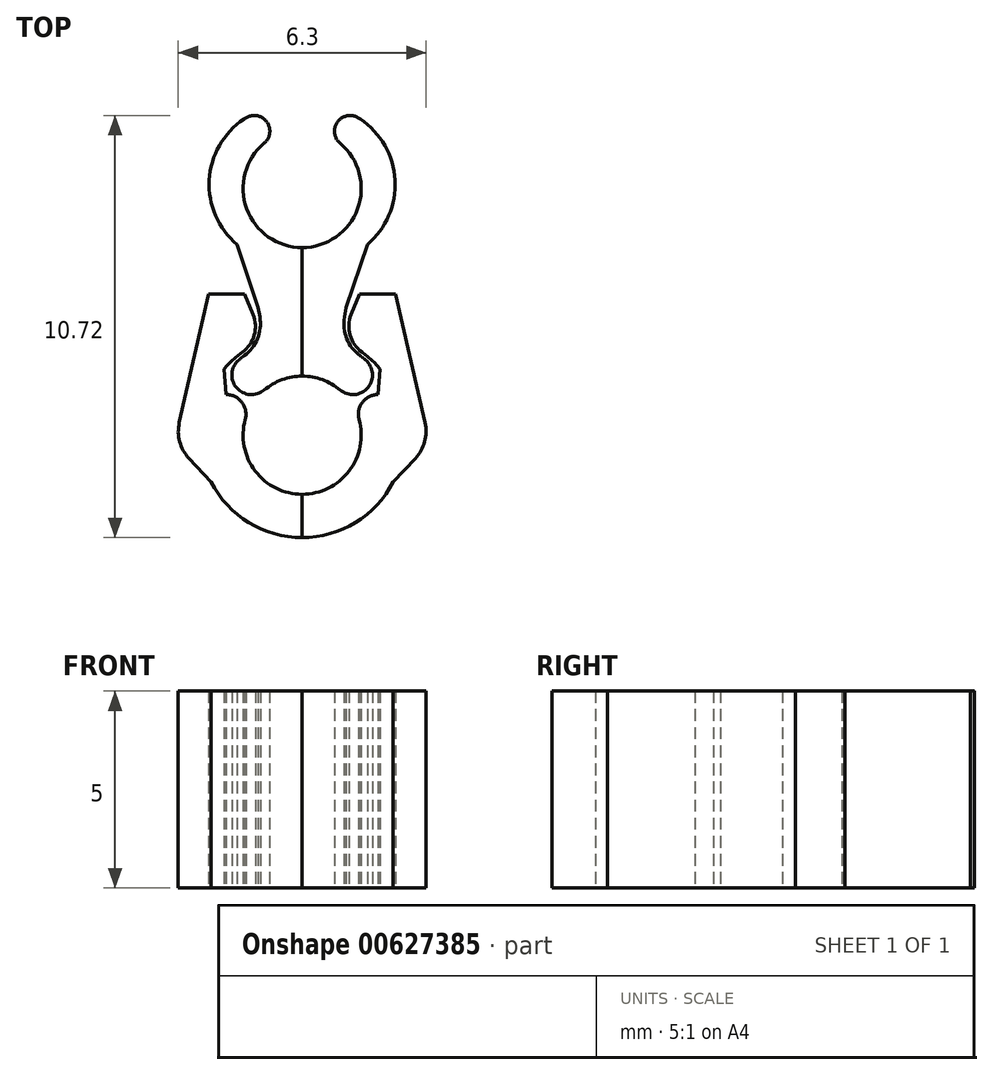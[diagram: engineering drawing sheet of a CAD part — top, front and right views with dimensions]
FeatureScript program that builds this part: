
annotation { "Feature Type Name" : "Feature", "Feature Type Description" : "" }
export const myFeature = defineFeature(function(context is Context, id is Id, definition is map)
    precondition{}
    {
        {
            var Q0;
            Q0=qCreatedBy(makeId("Top.planeOp"),FACE);
            var sketch = newSketch(context, id + "F0", { "sketchPlane" : qUnion([Q0])});
            skArc(sketch, "E0", {"start": v(-1.45, 0.4) * mm, "mid": v(-1.2, -0.9) * mm, "end": v(0, -1.5) * mm});
            skArc(sketch, "E1", {"start": v(-2.4, 0.67) * mm, "mid": v(-2.43, -0.6) * mm, "end": v(-1.82, -1.7) * mm});
            skPoint(sketch, "E2.orphan", {"position": v(0, 0.65) * mm});
            skLineSegment(sketch, "E3", {"start": v(0, 2) * mm, "end": v(0, 0) * mm});
            skArc(sketch, "E4.trimOffspring", {"start": v(-1.47, 2.02) * mm, "mid": v(-1.54, 1.97) * mm, "end": v(-1.6, 1.92) * mm});
            skArc(sketch, "E5.trimOffspring", {"start": v(0, 1.5) * mm, "mid": v(-0.51, 1.4) * mm, "end": v(-0.96, 1.15) * mm});
            skLineSegment(sketch, "E6", {"start": v(0, 0) * mm, "end": v(-0.96, 1.15) * mm, "construction": true});
            skArc(sketch, "E7", {"start": v(-1.6, 1.92) * mm, "mid": v(-1.67, 1.21) * mm, "end": v(-0.96, 1.15) * mm});
            skLineSegment(sketch, "E8", {"start": v(0, 0) * mm, "end": v(-2.4, 0.67) * mm, "construction": true});
            skArc(sketch, "E9", {"start": v(-1.45, 0.4) * mm, "mid": v(-1.53, 0.83) * mm, "end": v(-1.93, 1.03) * mm});
            skArc(sketch, "E10", {"start": v(-0.97, 2.41) * mm, "mid": v(-1.1, 2.35) * mm, "end": v(-1.23, 2.29) * mm});
            skPoint(sketch, "E11", {"position": v(0, 2.6) * mm});
            skLineSegment(sketch, "E12", {"start": v(-1.46, 3.59) * mm, "end": v(-1.25, 3.07) * mm, "construction": true});
            skLineSegment(sketch, "E13", {"start": v(-1.07, 3) * mm, "end": v(-1.12, 3.25) * mm});
            skLineSegment(sketch, "E14", {"start": v(-1.12, 3.25) * mm, "end": v(-3.54, 6.27) * mm, "construction": true});
            skLineSegment(sketch, "E15", {"start": v(-3.54, 6.27) * mm, "end": v(0.86, 6.27) * mm, "construction": true});
            skLineSegment(sketch, "E16", {"start": v(-1.46, 3.59) * mm, "end": v(-2.37, 3.59) * mm});
            skLineSegment(sketch, "E17", {"start": v(-2.37, 3.59) * mm, "end": v(-3.12, 0.32) * mm});
            skLineSegment(sketch, "E18", {"start": v(-2.88, -0.59) * mm, "end": v(-1.82, -1.7) * mm});
            skLineSegment(sketch, "E19", {"start": v(-0.98, 2.43) * mm, "end": v(-1.08, 2.65) * mm});
            skArc(sketch, "E20.trimOffspring", {"start": v(-1.52, 2.11) * mm, "mid": v(-1.76, 1.91) * mm, "end": v(-1.98, 1.68) * mm});
            skPoint(sketch, "E21.newPointB", {"position": v(-3.54, 8.6) * mm});
            skArc(sketch, "E21.filletArc", {"start": v(-1.52, 2.11) * mm, "mid": v(-1.22, 2.54) * mm, "end": v(-1.25, 3.07) * mm});
            skLineSegment(sketch, "E22", {"start": v(-1.99, 2.76) * mm, "end": v(-0.97, 2.13) * mm, "construction": true});
            skPoint(sketch, "E23", {"position": v(-1.3, 2.34) * mm});
            skArc(sketch, "E24.filletArc", {"start": v(-1.47, 2.02) * mm, "mid": v(-1.13, 2.45) * mm, "end": v(-1.07, 3) * mm});
            skPoint(sketch, "E25", {"position": v(-1.22, 2.28) * mm});
            skLineSegment(sketch, "E26.trimOffspring", {"start": v(-1.25, 3.07) * mm, "end": v(-1.46, 3.59) * mm});
            skLineSegment(sketch, "E27", {"start": v(0, 3.05) * mm, "end": v(0, 1.5) * mm});
            skPoint(sketch, "E28.visualSharp", {"position": v(-2.28, 1.03) * mm});
            skPoint(sketch, "E29.visualSharp", {"position": v(-3.24, -0.2) * mm});
            skArc(sketch, "E29.filletArc", {"start": v(-3.12, 0.32) * mm, "mid": v(-3.11, -0.16) * mm, "end": v(-2.88, -0.59) * mm});
            skArc(sketch, "E30", {"start": v(-0.96, 7.42) * mm, "mid": v(-0.63, 4.9) * mm, "end": v(1.5, 6.27) * mm});
            skLineSegment(sketch, "E31", {"start": v(-1.12, 3.25) * mm, "end": v(-1.66, 4.84) * mm});
            skLineSegment(sketch, "E32", {"start": v(0, 4.77) * mm, "end": v(0, 3.05) * mm});
            skLineSegment(sketch, "E33", {"start": v(0, 6.27) * mm, "end": v(-1.48, 8.03) * mm, "construction": true});
            skArc(sketch, "E34", {"start": v(-0.96, 7.42) * mm, "mid": v(-0.91, 7.98) * mm, "end": v(-1.48, 8.03) * mm});
            skLineSegment(sketch, "E35", {"start": v(0, 4.77) * mm, "end": v(0, 7.72) * mm});
            skArc(sketch, "E36.trimOffspring", {"start": v(-1.48, 8.03) * mm, "mid": v(-2.36, 6.48) * mm, "end": v(-1.66, 4.84) * mm});
            skLineSegment(sketch, "E37", {"start": v(0, -2.6) * mm, "end": v(0, -2.5) * mm});
            skArc(sketch, "E38.trimOffspring", {"start": v(0, 2.6) * mm, "mid": v(-0.5, 2.55) * mm, "end": v(-0.97, 2.41) * mm});
            skLineSegment(sketch, "E39.trimOffspring", {"start": v(0, -1.5) * mm, "end": v(0, -2.5) * mm});
            skLineSegment(sketch, "E40", {"start": v(-1.93, 1.03) * mm, "end": v(-1.98, 1.68) * mm});
            skArc(sketch, "E41.trimOffspring", {"start": v(-2.31, -1.19) * mm, "mid": v(-1.36, -2.22) * mm, "end": v(0, -2.6) * mm});
            skSolve(sketch);
        }
        {
            var Q0;
            {var subQ9=sQuery(id+"F0.wireOp",EDGE,"E4.trimOffspring");Q0=makeQuery(id+"F0.imprint","IMPRINT",FACE,{"disambiguationData":[TD([[makeQuery(id+"F0.imprint","IMPRINT",EDGE,{"derivedFrom":subQ9}),1.0]])]});}
            extrude(context, id + "F1", {"entities" : qUnion([Q0]), "depth" : 5 * mm, "offsetDistance" : 25 * mm});
        }
        {
            var Q0;
            Q0=makeQuery(id+"F0.imprint","IMPRINT",FACE,{"disambiguationData":[TD([[makeQuery(id+"F0.imprint","IMPRINT",EDGE,{"derivedFrom":sQuery(id+"F0.wireOp",EDGE,"E0")}),-1.0]])]});
            extrude(context, id + "F2", {"entities" : qUnion([Q0]), "depth" : 5 * mm, "offsetDistance" : 25 * mm});
        }
        {
            var Q0;
            Q0=makeQuery(id+"F0.imprint","IMPRINT",FACE,{"disambiguationData":[TD([[makeQuery(id+"F0.imprint","IMPRINT",EDGE,{"derivedFrom":sQuery(id+"F0.wireOp",EDGE,"E16")}),1.0]])]});
            extrude(context, id + "F3", {"entities" : qUnion([Q0]), "operationType" : NewBodyOperationType.ADD, "depth" : 5 * mm, "offsetDistance" : 25 * mm});
        }
        {
            var Q0;
            Q0=makeQuery(id+"F2.opExtrude","SWEPT_BODY",BODY,{"disambiguationData":[OSD([sQuery(id+"F0.wireOp",EDGE,"E0"),sQuery(id+"F0.wireOp",EDGE,"E9"),sQuery(id+"F0.wireOp",EDGE,"E16"),sQuery(id+"F0.wireOp",EDGE,"E17"),sQuery(id+"F0.wireOp",EDGE,"E18"),sQuery(id+"F0.wireOp",EDGE,"E21.filletArc"),sQuery(id+"F0.wireOp",EDGE,"E26.trimOffspring"),sQuery(id+"F0.wireOp",EDGE,"E29.filletArc"),sQuery(id+"F0.wireOp",EDGE,"E37"),sQuery(id+"F0.wireOp",EDGE,"E39.trimOffspring"),sQuery(id+"F0.wireOp",EDGE,"E20.trimOffspring"),sQuery(id+"F0.wireOp",EDGE,"E40"),sQuery(id+"F0.wireOp",EDGE,"E41.trimOffspring")])]});
            var Q1;
            Q1=qCreatedBy(makeId("Right.planeOp"),FACE);
            mirror(context, id + "F4", {"operationType" : NewBodyOperationType.ADD, "entities" : qUnion([Q0]), "mirrorPlane" : qUnion([Q1])});
        }
        {
            var Q0;
            Q0=makeQuery(id+"F1.opExtrude","SWEPT_BODY",BODY,{"disambiguationData":[OSD([sQuery(id+"F0.wireOp",EDGE,"E4.trimOffspring"),sQuery(id+"F0.wireOp",EDGE,"E5.trimOffspring"),sQuery(id+"F0.wireOp",EDGE,"E7"),sQuery(id+"F0.wireOp",EDGE,"E13"),sQuery(id+"F0.wireOp",EDGE,"E24.filletArc"),sQuery(id+"F0.wireOp",EDGE,"E27"),sQuery(id+"F0.wireOp",EDGE,"E30"),sQuery(id+"F0.wireOp",EDGE,"E31"),sQuery(id+"F0.wireOp",EDGE,"E32"),sQuery(id+"F0.wireOp",EDGE,"E34"),sQuery(id+"F0.wireOp",EDGE,"E36.trimOffspring")])]});
            var Q1;
            Q1=qCreatedBy(makeId("Right.planeOp"),FACE);
            mirror(context, id + "F5", {"operationType" : NewBodyOperationType.ADD, "entities" : qUnion([Q0]), "mirrorPlane" : qUnion([Q1])});
        }
    });
